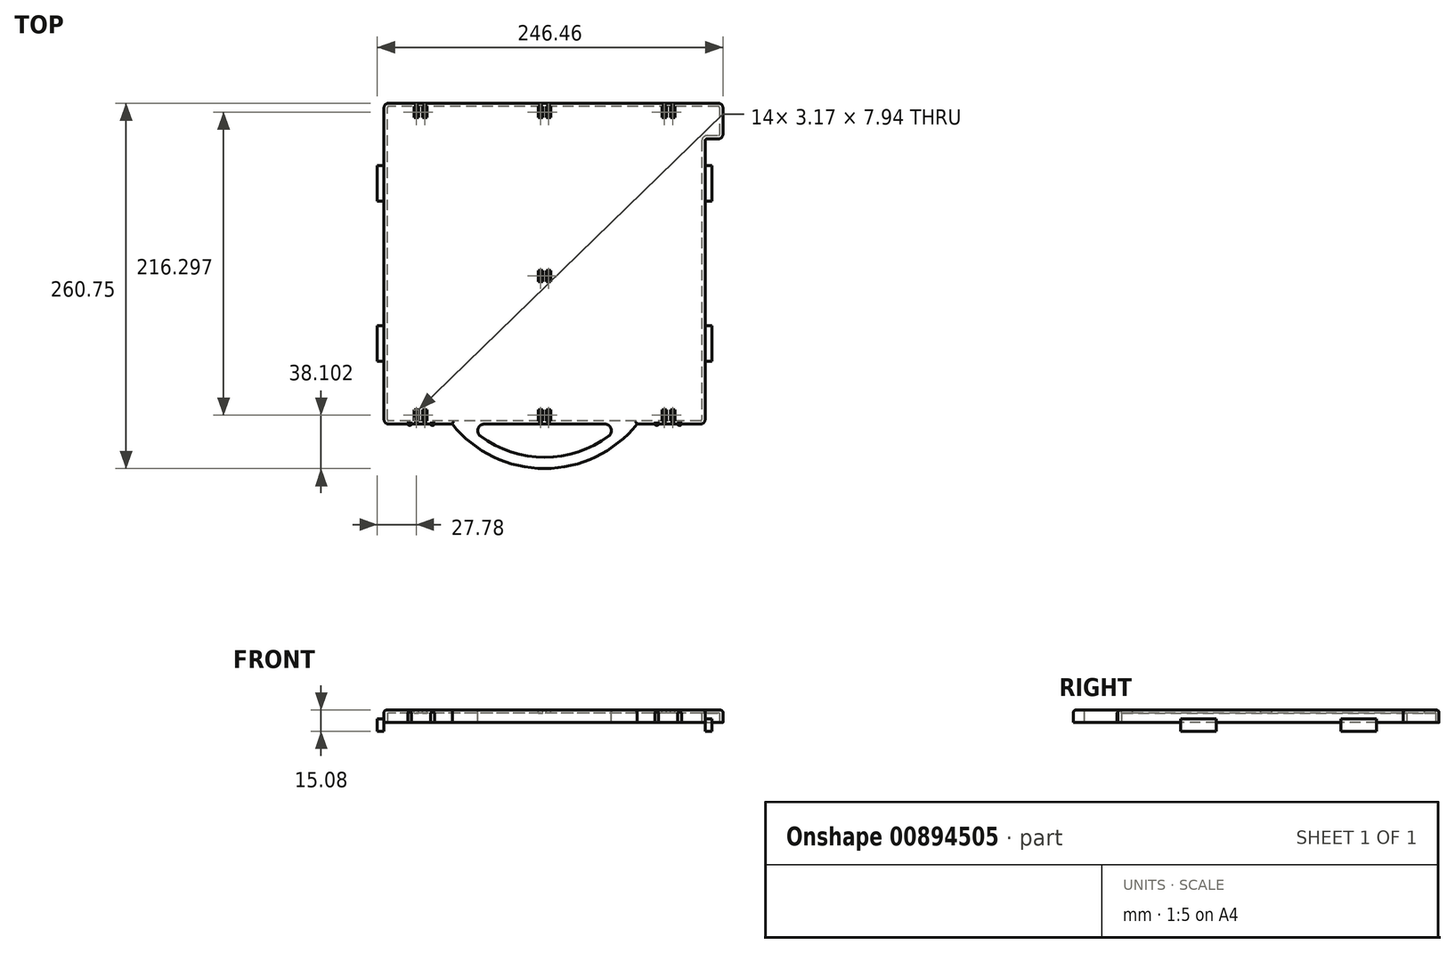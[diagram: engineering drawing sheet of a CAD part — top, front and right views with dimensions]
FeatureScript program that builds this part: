
annotation { "Feature Type Name" : "Feature", "Feature Type Description" : "" }
export const myFeature = defineFeature(function(context is Context, id is Id, definition is map)
    precondition{}
    {
        {
            var Q0;
            Q0=qCreatedBy(makeId("Top.planeOp"),FACE);
            var sketch = newSketch(context, id + "F0", { "sketchPlane" : qUnion([Q0])});
            skLineSegment(sketch, "E0.bottom", {"start": v(114.5, 114.5) * mm, "end": v(-114.5, 114.5) * mm});
            skLineSegment(sketch, "E0.top", {"start": v(114.5, -114.5) * mm, "end": v(-114.5, -114.5) * mm});
            skLineSegment(sketch, "E0.left", {"start": v(114.5, 114.5) * mm, "end": v(114.5, -114.5) * mm});
            skLineSegment(sketch, "E0.right", {"start": v(-114.5, 114.5) * mm, "end": v(-114.5, -114.5) * mm});
            skPoint(sketch, "E0.middle", {"position": v(0, 0) * mm});
            skLineSegment(sketch, "E1.bottom", {"start": v(114.5, 114.5) * mm, "end": v(127.2, 114.5) * mm});
            skLineSegment(sketch, "E1.top", {"start": v(114.5, 89.1) * mm, "end": v(127.2, 89.1) * mm});
            skLineSegment(sketch, "E1.left", {"start": v(114.5, 114.5) * mm, "end": v(114.5, 89.1) * mm});
            skLineSegment(sketch, "E1.right", {"start": v(127.2, 114.5) * mm, "end": v(127.2, 89.1) * mm});
            skSolve(sketch);
        }
        {
            var Q0;
            Q0 = qSketchRegion(id + "F0", true);
            extrude(context, id + "F1", {"entities" : qUnion([Q0]), "depth" : 8.9 * mm, "offsetDistance" : 25 * mm});
        }
        {
            var Q0;
            Q0=makeQuery(id+"F1.opExtrude","SWEPT_EDGE",EDGE,{"disambiguationData":[OSD([sQuery(id+"F0.wireOp",EDGE,"E1.bottom"),sQuery(id+"F0.wireOp",EDGE,"E1.right")])]});
            var Q1;
            Q1=makeQuery(id+"F1.opExtrude","SWEPT_EDGE",EDGE,{"disambiguationData":[OSD([sQuery(id+"F0.wireOp",EDGE,"E1.top"),sQuery(id+"F0.wireOp",EDGE,"E1.right")])]});
            var Q2;
            Q2=makeQuery(id+"F1.opExtrude","SWEPT_EDGE",EDGE,{"disambiguationData":[OSD([sQuery(id+"F0.wireOp",EDGE,"E0.bottom"),sQuery(id+"F0.wireOp",EDGE,"E0.right")])]});
            var Q3;
            Q3=makeQuery(id+"F1.opExtrude","SWEPT_EDGE",EDGE,{"disambiguationData":[OSD([sQuery(id+"F0.wireOp",EDGE,"E0.top"),sQuery(id+"F0.wireOp",EDGE,"E0.right")])]});
            var Q4;
            Q4=makeQuery(id+"F1.opExtrude","SWEPT_EDGE",EDGE,{"disambiguationData":[OSD([sQuery(id+"F0.wireOp",EDGE,"E0.top"),sQuery(id+"F0.wireOp",EDGE,"E0.left")])]});
            fillet(context, id + "F2", {"entities" : qUnion([Q0, Q1, Q2, Q3, Q4]), "radius" : 3.17 * mm, "tangentPropagation" : true, "allowEdgeOverflow" : false});
        }
        {
            var Q0;
            Q0=makeQuery(id+"F1.opExtrude","SWEPT_EDGE",EDGE,{"disambiguationData":[OSD([sQuery(id+"F0.wireOp",EDGE,"E0.left"),sQuery(id+"F0.wireOp",EDGE,"E1.top"),sQuery(id+"F0.wireOp",EDGE,"E1.left")])]});
            fillet(context, id + "F3", {"entities" : qUnion([Q0]), "radius" : 1.59 * mm, "tangentPropagation" : true, "allowEdgeOverflow" : false});
        }
        {
            var Q0;
            Q0=makeQuery(id+"F1.opExtrude","CAP_FACE",FACE,{"disambiguationData":[OSD([sQuery(id+"F0.wireOp",EDGE,"E0.bottom"),sQuery(id+"F0.wireOp",EDGE,"E0.top"),sQuery(id+"F0.wireOp",EDGE,"E0.left"),sQuery(id+"F0.wireOp",EDGE,"E0.right"),sQuery(id+"F0.wireOp",EDGE,"E1.bottom"),sQuery(id+"F0.wireOp",EDGE,"E1.top"),sQuery(id+"F0.wireOp",EDGE,"E1.right")])],"isStart":false});
            var sketch = newSketch(context, id + "F4", { "sketchPlane" : qUnion([Q0])});
            skLineSegment(sketch, "E2", {"start": v(0, 0) * mm, "end": v(0, 114.5) * mm, "construction": true});
            skLineSegment(sketch, "E3", {"start": v(0, 0) * mm, "end": v(0, -114.5) * mm, "construction": true});
            skLineSegment(sketch, "E4.bottom", {"start": v(-1.39, 112.12) * mm, "end": v(-4.56, 112.12) * mm});
            skLineSegment(sketch, "E4.top", {"start": v(-1.39, 104.18) * mm, "end": v(-4.56, 104.18) * mm});
            skLineSegment(sketch, "E4.left", {"start": v(-1.39, 112.12) * mm, "end": v(-1.39, 104.18) * mm});
            skLineSegment(sketch, "E4.right", {"start": v(-4.56, 112.12) * mm, "end": v(-4.56, 104.18) * mm});
            skLineSegment(sketch, "E5", {"start": v(-4.56, 112.12) * mm, "end": v(-83.94, 112.12) * mm, "construction": true});
            skLineSegment(sketch, "E6.bottom", {"start": v(-83.94, 112.12) * mm, "end": v(-87.11, 112.12) * mm});
            skLineSegment(sketch, "E6.top", {"start": v(-83.94, 104.18) * mm, "end": v(-87.11, 104.18) * mm});
            skLineSegment(sketch, "E6.left", {"start": v(-83.94, 112.12) * mm, "end": v(-83.94, 104.18) * mm});
            skLineSegment(sketch, "E6.right", {"start": v(-87.11, 112.12) * mm, "end": v(-87.11, 104.18) * mm});
            skLineSegment(sketch, "E7.bottom", {"start": v(-89.9, 112.12) * mm, "end": v(-93.07, 112.12) * mm});
            skLineSegment(sketch, "E7.top", {"start": v(-89.9, 104.18) * mm, "end": v(-93.07, 104.18) * mm});
            skLineSegment(sketch, "E7.left", {"start": v(-89.9, 112.12) * mm, "end": v(-89.9, 104.18) * mm});
            skLineSegment(sketch, "E7.right", {"start": v(-93.07, 112.12) * mm, "end": v(-93.07, 104.18) * mm});
            skLineSegment(sketch, "E8.MirrorCS", {"start": v(83.94, 112.12) * mm, "end": v(87.11, 112.12) * mm});
            skLineSegment(sketch, "E9.MirrorCS", {"start": v(1.39, 112.12) * mm, "end": v(4.56, 112.12) * mm});
            skLineSegment(sketch, "E10.MirrorCS", {"start": v(1.39, 112.12) * mm, "end": v(1.39, 104.18) * mm});
            skLineSegment(sketch, "E11.MirrorCS", {"start": v(89.9, 104.18) * mm, "end": v(93.07, 104.18) * mm});
            skLineSegment(sketch, "E12.MirrorCS", {"start": v(89.9, 112.12) * mm, "end": v(89.9, 104.18) * mm});
            skLineSegment(sketch, "E13.MirrorCS", {"start": v(4.56, 112.12) * mm, "end": v(4.56, 104.18) * mm});
            skLineSegment(sketch, "E14.MirrorCS", {"start": v(89.9, 112.12) * mm, "end": v(93.07, 112.12) * mm});
            skLineSegment(sketch, "E15.MirrorCS", {"start": v(83.94, 104.18) * mm, "end": v(87.11, 104.18) * mm});
            skLineSegment(sketch, "E16.MirrorCS", {"start": v(83.94, 112.12) * mm, "end": v(83.94, 104.18) * mm});
            skLineSegment(sketch, "E17.MirrorCS", {"start": v(87.11, 112.12) * mm, "end": v(87.11, 104.18) * mm});
            skLineSegment(sketch, "E18.MirrorCS", {"start": v(93.07, 112.12) * mm, "end": v(93.07, 104.18) * mm});
            skLineSegment(sketch, "E19.MirrorCS", {"start": v(1.39, 104.18) * mm, "end": v(4.56, 104.18) * mm});
            skLineSegment(sketch, "E20.MirrorCS", {"start": v(4.56, 112.12) * mm, "end": v(83.94, 112.12) * mm, "construction": true});
            skLineSegment(sketch, "E21", {"start": v(0, 0) * mm, "end": v(114.5, 0) * mm, "construction": true});
            skLineSegment(sketch, "E22.MirrorCS", {"start": v(-1.39, -104.18) * mm, "end": v(-4.56, -104.18) * mm});
            skLineSegment(sketch, "E23.MirrorCS", {"start": v(-83.94, -104.18) * mm, "end": v(-87.11, -104.18) * mm});
            skLineSegment(sketch, "E24.MirrorCS", {"start": v(1.39, -104.18) * mm, "end": v(4.56, -104.18) * mm});
            skLineSegment(sketch, "E25.MirrorCS", {"start": v(-1.39, -112.12) * mm, "end": v(-4.56, -112.12) * mm});
            skLineSegment(sketch, "E26.MirrorCS", {"start": v(-83.94, -112.12) * mm, "end": v(-87.11, -112.12) * mm});
            skLineSegment(sketch, "E27.MirrorCS", {"start": v(-87.11, -112.12) * mm, "end": v(-87.11, -104.18) * mm});
            skLineSegment(sketch, "E28.MirrorCS", {"start": v(-4.56, -112.12) * mm, "end": v(-4.56, -104.18) * mm});
            skLineSegment(sketch, "E29.MirrorCS", {"start": v(-89.9, -112.12) * mm, "end": v(-89.9, -104.18) * mm});
            skLineSegment(sketch, "E30.MirrorCS", {"start": v(83.94, -112.12) * mm, "end": v(87.11, -112.12) * mm});
            skLineSegment(sketch, "E31.MirrorCS", {"start": v(-83.94, -112.12) * mm, "end": v(-83.94, -104.18) * mm});
            skLineSegment(sketch, "E32.MirrorCS", {"start": v(1.39, -112.12) * mm, "end": v(4.56, -112.12) * mm});
            skLineSegment(sketch, "E33.MirrorCS", {"start": v(-89.9, -112.12) * mm, "end": v(-93.07, -112.12) * mm});
            skLineSegment(sketch, "E34.MirrorCS", {"start": v(1.39, -112.12) * mm, "end": v(1.39, -104.18) * mm});
            skLineSegment(sketch, "E35.MirrorCS", {"start": v(4.56, -112.12) * mm, "end": v(4.56, -104.18) * mm});
            skLineSegment(sketch, "E36.MirrorCS", {"start": v(-1.39, -112.12) * mm, "end": v(-1.39, -104.18) * mm});
            skLineSegment(sketch, "E37.MirrorCS", {"start": v(89.9, -104.18) * mm, "end": v(93.07, -104.18) * mm});
            skLineSegment(sketch, "E38.MirrorCS", {"start": v(89.9, -112.12) * mm, "end": v(89.9, -104.18) * mm});
            skLineSegment(sketch, "E39.MirrorCS", {"start": v(93.07, -112.12) * mm, "end": v(93.07, -104.18) * mm});
            skLineSegment(sketch, "E40.MirrorCS", {"start": v(83.94, -104.18) * mm, "end": v(87.11, -104.18) * mm});
            skLineSegment(sketch, "E41.MirrorCS", {"start": v(89.9, -112.12) * mm, "end": v(93.07, -112.12) * mm});
            skLineSegment(sketch, "E42.MirrorCS", {"start": v(83.94, -112.12) * mm, "end": v(83.94, -104.18) * mm});
            skLineSegment(sketch, "E43.MirrorCS", {"start": v(-89.9, -104.18) * mm, "end": v(-93.07, -104.18) * mm});
            skLineSegment(sketch, "E44.MirrorCS", {"start": v(-93.07, -112.12) * mm, "end": v(-93.07, -104.18) * mm});
            skLineSegment(sketch, "E45.MirrorCS", {"start": v(87.11, -112.12) * mm, "end": v(87.11, -104.18) * mm});
            skLineSegment(sketch, "E46.MirrorCS", {"start": v(-4.56, -112.12) * mm, "end": v(-83.94, -112.12) * mm, "construction": true});
            skLineSegment(sketch, "E47.MirrorCS", {"start": v(4.56, -112.12) * mm, "end": v(83.94, -112.12) * mm, "construction": true});
            skLineSegment(sketch, "E48.MirrorCS", {"start": v(-1.39, -4.8) * mm, "end": v(-4.56, -4.8) * mm});
            skLineSegment(sketch, "E49.MirrorCS", {"start": v(1.39, -4.8) * mm, "end": v(4.56, -4.8) * mm});
            skLineSegment(sketch, "E50.MirrorCS", {"start": v(-1.39, -12.74) * mm, "end": v(-4.56, -12.74) * mm});
            skLineSegment(sketch, "E51.MirrorCS", {"start": v(-4.56, -12.74) * mm, "end": v(-4.56, -4.8) * mm});
            skLineSegment(sketch, "E52.MirrorCS", {"start": v(1.39, -12.74) * mm, "end": v(4.56, -12.74) * mm});
            skLineSegment(sketch, "E53.MirrorCS", {"start": v(1.39, -12.74) * mm, "end": v(1.39, -4.8) * mm});
            skLineSegment(sketch, "E54.MirrorCS", {"start": v(4.56, -12.74) * mm, "end": v(4.56, -4.8) * mm});
            skLineSegment(sketch, "E55.MirrorCS", {"start": v(-1.39, -12.74) * mm, "end": v(-1.39, -4.8) * mm});
            skLineSegment(sketch, "E56", {"start": v(-1.39, -8.77) * mm, "end": v(1.39, -8.77) * mm, "construction": true});
            skPoint(sketch, "E57", {"position": v(0, -8.77) * mm});
            skLineSegment(sketch, "E58", {"start": v(-1.39, 108.15) * mm, "end": v(1.39, 108.15) * mm, "construction": true});
            skSolve(sketch);
        }
        {
            var Q0;
            Q0 = qSketchRegion(id + "F4", true);
            extrude(context, id + "F5", {"entities" : qUnion([Q0]), "operationType" : NewBodyOperationType.REMOVE, "endBound" : BoundingType.THROUGH_ALL, "oppositeDirection" : true, "depth" : 25.4 * mm, "offsetDistance" : 25.4 * mm});
        }
        {
            var Q0;
            Q0=makeQuery(id+"F1.opExtrude","SWEPT_FACE",FACE,{"disambiguationData":[OSD([sQuery(id+"F0.wireOp",EDGE,"E0.top")])]});
            var sketch = newSketch(context, id + "F6", { "sketchPlane" : qUnion([Q0])});
            skLineSegment(sketch, "E59.bottom", {"start": v(-97.63, 0) * mm, "end": v(-94.85, 0) * mm});
            skLineSegment(sketch, "E59.top", {"start": v(-97.63, 7.34) * mm, "end": v(-94.85, 7.34) * mm});
            skLineSegment(sketch, "E59.left", {"start": v(-97.63, 0) * mm, "end": v(-97.63, 7.34) * mm});
            skLineSegment(sketch, "E59.right", {"start": v(-94.85, 0) * mm, "end": v(-94.85, 7.34) * mm});
            skLineSegment(sketch, "E60.bottom", {"start": v(-81.36, 0) * mm, "end": v(-78.58, 0) * mm});
            skLineSegment(sketch, "E60.top", {"start": v(-81.36, 7.34) * mm, "end": v(-78.58, 7.34) * mm});
            skLineSegment(sketch, "E60.left", {"start": v(-81.36, 0) * mm, "end": v(-81.36, 7.34) * mm});
            skLineSegment(sketch, "E60.right", {"start": v(-78.58, 0) * mm, "end": v(-78.58, 7.34) * mm});
            skLineSegment(sketch, "E61", {"start": v(0, 0) * mm, "end": v(0, 8.9) * mm, "construction": true});
            skLineSegment(sketch, "E62.MirrorCS", {"start": v(97.63, 0) * mm, "end": v(94.85, 0) * mm});
            skLineSegment(sketch, "E63.MirrorCS", {"start": v(81.36, 0) * mm, "end": v(78.58, 0) * mm});
            skLineSegment(sketch, "E64.MirrorCS", {"start": v(94.85, 0) * mm, "end": v(94.85, 7.34) * mm});
            skLineSegment(sketch, "E65.MirrorCS", {"start": v(81.36, 7.34) * mm, "end": v(78.58, 7.34) * mm});
            skLineSegment(sketch, "E66.MirrorCS", {"start": v(78.58, 0) * mm, "end": v(78.58, 7.34) * mm});
            skLineSegment(sketch, "E67.MirrorCS", {"start": v(81.36, 0) * mm, "end": v(81.36, 7.34) * mm});
            skLineSegment(sketch, "E68.MirrorCS", {"start": v(97.63, 0) * mm, "end": v(97.63, 7.34) * mm});
            skLineSegment(sketch, "E69.MirrorCS", {"start": v(97.63, 7.34) * mm, "end": v(94.85, 7.34) * mm});
            skSolve(sketch);
        }
        {
            var Q0;
            Q0 = qSketchRegion(id + "F6", true);
            extrude(context, id + "F7", {"entities" : qUnion([Q0]), "operationType" : NewBodyOperationType.ADD, "depth" : 0.8 * mm, "offsetDistance" : 25.4 * mm});
        }
        {
            var Q0;
            Q0=makeQuery(id+"F7.opExtrude","CAP_EDGE",EDGE,{"disambiguationData":[OSD([sQuery(id+"F6.wireOp",EDGE,"E66.MirrorCS")])],"isStart":false});
            var Q1;
            Q1=makeQuery(id+"F7.opExtrude","CAP_EDGE",EDGE,{"disambiguationData":[OSD([sQuery(id+"F6.wireOp",EDGE,"E67.MirrorCS")])],"isStart":false});
            var Q2;
            Q2=makeQuery(id+"F7.opExtrude","SWEPT_EDGE",EDGE,{"disambiguationData":[OSD([sQuery(id+"F6.wireOp",EDGE,"E65.MirrorCS"),sQuery(id+"F6.wireOp",EDGE,"E67.MirrorCS")])]});
            var Q3;
            Q3=makeQuery(id+"F7.opExtrude","SWEPT_EDGE",EDGE,{"disambiguationData":[OSD([sQuery(id+"F6.wireOp",EDGE,"E65.MirrorCS"),sQuery(id+"F6.wireOp",EDGE,"E66.MirrorCS")])]});
            var Q4;
            Q4=makeQuery(id+"F7.opExtrude","CAP_EDGE",EDGE,{"disambiguationData":[OSD([sQuery(id+"F6.wireOp",EDGE,"E65.MirrorCS")])],"isStart":false});
            var Q5;
            Q5=makeQuery(id+"F7.opExtrude","SWEPT_EDGE",EDGE,{"disambiguationData":[OSD([sQuery(id+"F6.wireOp",EDGE,"E68.MirrorCS"),sQuery(id+"F6.wireOp",EDGE,"E69.MirrorCS")])]});
            var Q6;
            Q6=makeQuery(id+"F7.opExtrude","SWEPT_EDGE",EDGE,{"disambiguationData":[OSD([sQuery(id+"F6.wireOp",EDGE,"E64.MirrorCS"),sQuery(id+"F6.wireOp",EDGE,"E69.MirrorCS")])]});
            var Q7;
            Q7=makeQuery(id+"F7.opExtrude","CAP_EDGE",EDGE,{"disambiguationData":[OSD([sQuery(id+"F6.wireOp",EDGE,"E69.MirrorCS")])],"isStart":false});
            var Q8;
            Q8=makeQuery(id+"F7.opExtrude","CAP_EDGE",EDGE,{"disambiguationData":[OSD([sQuery(id+"F6.wireOp",EDGE,"E68.MirrorCS")])],"isStart":false});
            var Q9;
            Q9=makeQuery(id+"F7.opExtrude","CAP_EDGE",EDGE,{"disambiguationData":[OSD([sQuery(id+"F6.wireOp",EDGE,"E64.MirrorCS")])],"isStart":false});
            var Q10;
            Q10=makeQuery(id+"F7.opExtrude","SWEPT_EDGE",EDGE,{"disambiguationData":[OSD([sQuery(id+"F6.wireOp",EDGE,"E59.top"),sQuery(id+"F6.wireOp",EDGE,"E59.left")])]});
            var Q11;
            Q11=makeQuery(id+"F7.opExtrude","SWEPT_EDGE",EDGE,{"disambiguationData":[OSD([sQuery(id+"F6.wireOp",EDGE,"E59.top"),sQuery(id+"F6.wireOp",EDGE,"E59.right")])]});
            var Q12;
            Q12=makeQuery(id+"F7.opExtrude","SWEPT_EDGE",EDGE,{"disambiguationData":[OSD([sQuery(id+"F6.wireOp",EDGE,"E60.top"),sQuery(id+"F6.wireOp",EDGE,"E60.left")])]});
            var Q13;
            Q13=makeQuery(id+"F7.opExtrude","SWEPT_EDGE",EDGE,{"disambiguationData":[OSD([sQuery(id+"F6.wireOp",EDGE,"E60.top"),sQuery(id+"F6.wireOp",EDGE,"E60.right")])]});
            var Q14;
            Q14=makeQuery(id+"F7.opExtrude","CAP_EDGE",EDGE,{"disambiguationData":[OSD([sQuery(id+"F6.wireOp",EDGE,"E60.top")])],"isStart":false});
            var Q15;
            Q15=makeQuery(id+"F7.opExtrude","CAP_EDGE",EDGE,{"disambiguationData":[OSD([sQuery(id+"F6.wireOp",EDGE,"E59.top")])],"isStart":false});
            var Q16;
            Q16=makeQuery(id+"F7.opExtrude","CAP_EDGE",EDGE,{"disambiguationData":[OSD([sQuery(id+"F6.wireOp",EDGE,"E59.left")])],"isStart":false});
            var Q17;
            Q17=makeQuery(id+"F7.opExtrude","CAP_EDGE",EDGE,{"disambiguationData":[OSD([sQuery(id+"F6.wireOp",EDGE,"E60.left")])],"isStart":false});
            var Q18;
            Q18=makeQuery(id+"F7.opExtrude","CAP_EDGE",EDGE,{"disambiguationData":[OSD([sQuery(id+"F6.wireOp",EDGE,"E60.right")])],"isStart":false});
            var Q19;
            Q19=makeQuery(id+"F7.opExtrude","CAP_EDGE",EDGE,{"disambiguationData":[OSD([sQuery(id+"F6.wireOp",EDGE,"E59.right")])],"isStart":false});
            fillet(context, id + "F8", {"entities" : qUnion([Q0, Q1, Q2, Q3, Q4, Q5, Q6, Q7, Q8, Q9, Q10, Q11, Q12, Q13, Q14, Q15, Q16, Q17, Q18, Q19]), "radius" : 0.8 * mm, "tangentPropagation" : true, "allowEdgeOverflow" : false});
        }
        {
            var Q0;
            Q0=makeQuery(id+"F1.opExtrude","SWEPT_FACE",FACE,{"disambiguationData":[OSD([sQuery(id+"F0.wireOp",EDGE,"E0.left")])]});
            var sketch = newSketch(context, id + "F9", { "sketchPlane" : qUnion([Q0])});
            skLineSegment(sketch, "E70.bottom", {"start": v(44.65, 2.54) * mm, "end": v(70.05, 2.54) * mm});
            skLineSegment(sketch, "E70.top", {"start": v(44.65, -6.2) * mm, "end": v(70.05, -6.2) * mm});
            skLineSegment(sketch, "E70.left", {"start": v(44.65, 2.54) * mm, "end": v(44.65, -6.2) * mm});
            skLineSegment(sketch, "E70.right", {"start": v(70.05, 2.54) * mm, "end": v(70.05, -6.2) * mm});
            skLineSegment(sketch, "E71.bottom", {"start": v(-69.65, 2.54) * mm, "end": v(-44.25, 2.54) * mm});
            skLineSegment(sketch, "E71.top", {"start": v(-69.65, -6.2) * mm, "end": v(-44.25, -6.2) * mm});
            skLineSegment(sketch, "E71.left", {"start": v(-69.65, 2.54) * mm, "end": v(-69.65, -6.2) * mm});
            skLineSegment(sketch, "E71.right", {"start": v(-44.25, 2.54) * mm, "end": v(-44.25, -6.2) * mm});
            skLineSegment(sketch, "E72", {"start": v(44.65, 2.54) * mm, "end": v(-44.25, 2.54) * mm, "construction": true});
            skSolve(sketch);
        }
        {
            var Q0;
            Q0 = qSketchRegion(id + "F9", true);
            extrude(context, id + "F10", {"entities" : qUnion([Q0]), "operationType" : NewBodyOperationType.ADD, "depth" : 4.76 * mm, "offsetDistance" : 25.4 * mm});
        }
        {
            var Q0;
            Q0=makeQuery(id+"F1.opExtrude","SWEPT_FACE",FACE,{"disambiguationData":[OSD([sQuery(id+"F0.wireOp",EDGE,"E0.right")])]});
            var sketch = newSketch(context, id + "F11", { "sketchPlane" : qUnion([Q0])});
            skLineSegment(sketch, "E73.0", {"start": v(-44.65, 2.54) * mm, "end": v(-70.05, 2.54) * mm});
            skLineSegment(sketch, "E73.1", {"start": v(-44.65, -6.2) * mm, "end": v(-70.05, -6.2) * mm});
            skLineSegment(sketch, "E73.2", {"start": v(-44.65, 2.54) * mm, "end": v(-44.65, -6.2) * mm});
            skLineSegment(sketch, "E73.3", {"start": v(-70.05, 2.54) * mm, "end": v(-70.05, -6.2) * mm});
            skLineSegment(sketch, "E73.4", {"start": v(69.65, 2.54) * mm, "end": v(44.25, 2.54) * mm});
            skLineSegment(sketch, "E73.5", {"start": v(69.65, -6.2) * mm, "end": v(44.25, -6.2) * mm});
            skLineSegment(sketch, "E73.6", {"start": v(69.65, 2.54) * mm, "end": v(69.65, -6.2) * mm});
            skLineSegment(sketch, "E73.7", {"start": v(44.25, 2.54) * mm, "end": v(44.25, -6.2) * mm});
            skLineSegment(sketch, "E73.8", {"start": v(-44.65, 2.54) * mm, "end": v(44.25, 2.54) * mm});
            skSolve(sketch);
        }
        {
            var Q0;
            Q0 = qSketchRegion(id + "F11", true);
            extrude(context, id + "F12", {"entities" : qUnion([Q0]), "operationType" : NewBodyOperationType.ADD, "depth" : 4.76 * mm, "offsetDistance" : 25.4 * mm});
        }
        {
            var Q0;
            Q0=makeQuery(id+"F1.opExtrude","CAP_FACE",FACE,{"disambiguationData":[OSD([sQuery(id+"F0.wireOp",EDGE,"E0.bottom"),sQuery(id+"F0.wireOp",EDGE,"E0.top"),sQuery(id+"F0.wireOp",EDGE,"E0.left"),sQuery(id+"F0.wireOp",EDGE,"E0.right"),sQuery(id+"F0.wireOp",EDGE,"E1.bottom"),sQuery(id+"F0.wireOp",EDGE,"E1.top"),sQuery(id+"F0.wireOp",EDGE,"E1.right")])],"isStart":false});
            var sketch = newSketch(context, id + "F13", { "sketchPlane" : qUnion([Q0])});
            skPoint(sketch, "E74.0", {"position": v(-78.58, -114.5) * mm});
            skPoint(sketch, "E75.0", {"position": v(78.58, -114.5) * mm});
            skLineSegment(sketch, "E76", {"start": v(-78.58, -114.5) * mm, "end": v(-65.88, -114.5) * mm});
            skLineSegment(sketch, "E77", {"start": v(78.58, -114.5) * mm, "end": v(65.88, -114.5) * mm});
            skLineSegment(sketch, "E78.bottom", {"start": v(-65.88, -114.5) * mm, "end": v(65.88, -114.5) * mm});
            skLineSegment(sketch, "E78.top", {"start": v(-65.88, -146.25) * mm, "end": v(65.88, -146.25) * mm});
            skLineSegment(sketch, "E78.left", {"start": v(-65.88, -114.5) * mm, "end": v(-65.88, -146.25) * mm});
            skLineSegment(sketch, "E78.right", {"start": v(65.88, -114.5) * mm, "end": v(65.88, -146.25) * mm});
            skLineSegment(sketch, "E79", {"start": v(0, -146.25) * mm, "end": v(0, -62.02) * mm, "construction": true});
            skLineSegment(sketch, "E80", {"start": v(0, -62.02) * mm, "end": v(-65.88, -114.5) * mm, "construction": true});
            skLineSegment(sketch, "E81", {"start": v(0, -62.02) * mm, "end": v(65.88, -114.5) * mm, "construction": true});
            skArc(sketch, "E82", {"start": v(65.88, -114.5) * mm, "mid": v(0, -146.25) * mm, "end": v(-65.88, -114.5) * mm});
            skLineSegment(sketch, "E83", {"start": v(0, -62.02) * mm, "end": v(0, -138.31) * mm, "construction": true});
            skArc(sketch, "E84", {"start": v(0, -138.31) * mm, "mid": v(30.14, -132.1) * mm, "end": v(55.37, -114.5) * mm});
            skArc(sketch, "E85", {"start": v(0, -138.31) * mm, "mid": v(-30.14, -132.1) * mm, "end": v(-55.37, -114.5) * mm});
            skSolve(sketch);
        }
        {
            var Q0;
            {var subQ6=sQuery(id+"F13.wireOp",EDGE,"E84");Q0=makeQuery(id+"F13.imprint","IMPRINT",FACE,{"disambiguationData":[TD([[makeQuery(id+"F13.imprint","IMPRINT",EDGE,{"derivedFrom":subQ6}),-1.0]])]});}
            var Q1;
            Q1=makeQuery(id+"F7.boolean.opBoolean","MERGE",FACE,{"derivedFrom":[makeQuery(id+"F1.opExtrude","CAP_FACE",FACE,{"disambiguationData":[OSD([sQuery(id+"F0.wireOp",EDGE,"E0.bottom"),sQuery(id+"F0.wireOp",EDGE,"E0.top"),sQuery(id+"F0.wireOp",EDGE,"E0.left"),sQuery(id+"F0.wireOp",EDGE,"E0.right"),sQuery(id+"F0.wireOp",EDGE,"E1.bottom"),sQuery(id+"F0.wireOp",EDGE,"E1.top"),sQuery(id+"F0.wireOp",EDGE,"E1.right")])],"isStart":true}),makeQuery(id+"F7.opExtrude","SWEPT_FACE",FACE,{"disambiguationData":[OSD([sQuery(id+"F6.wireOp",EDGE,"E59.bottom")])]}),makeQuery(id+"F7.opExtrude","SWEPT_FACE",FACE,{"disambiguationData":[OSD([sQuery(id+"F6.wireOp",EDGE,"E60.bottom")])]}),makeQuery(id+"F7.opExtrude","SWEPT_FACE",FACE,{"disambiguationData":[OSD([sQuery(id+"F6.wireOp",EDGE,"E62.MirrorCS")])]}),makeQuery(id+"F7.opExtrude","SWEPT_FACE",FACE,{"disambiguationData":[OSD([sQuery(id+"F6.wireOp",EDGE,"E63.MirrorCS")])]})]});
            extrude(context, id + "F14", {"entities" : qUnion([Q0]), "operationType" : NewBodyOperationType.ADD, "endBound" : BoundingType.UP_TO_SURFACE, "oppositeDirection" : true, "depth" : 25.4 * mm, "endBoundEntityFace" : qUnion([Q1]), "offsetDistance" : 25.4 * mm});
        }
        {
            var Q0;
            Q0=makeQuery(id+"F14.opExtrude","SWEPT_EDGE",EDGE,{"disambiguationData":[OSD([sQuery(id+"F13.wireOp",EDGE,"E78.bottom"),sQuery(id+"F13.wireOp",EDGE,"E85")])]});
            var Q1;
            Q1=makeQuery(id+"F14.opExtrude","SWEPT_EDGE",EDGE,{"disambiguationData":[OSD([sQuery(id+"F13.wireOp",EDGE,"E78.bottom"),sQuery(id+"F13.wireOp",EDGE,"E84")])]});
            fillet(context, id + "F15", {"entities" : qUnion([Q0, Q1]), "radius" : 4.76 * mm, "tangentPropagation" : true, "allowEdgeOverflow" : false});
        }
        {
            var Q0;
            Q0=makeQuery(id+"F14.opExtrude","CAP_EDGE",EDGE,{"disambiguationData":[OSD([sQuery(id+"F13.wireOp",EDGE,"E84"),sQuery(id+"F13.wireOp",EDGE,"E85")])],"isStart":true});
            var Q1;
            {var subQ1=sQuery(id+"F0.wireOp",EDGE,"E0.left");var subQ2=sQuery(id+"F0.wireOp",EDGE,"E0.top");Q1=makeQuery(id+"F14.boolean.opBoolean","SPLIT",EDGE,{"disambiguationData":[TD([makeQuery(id+"F2.opFillet","BLEND_FACE",FACE,{"disambiguationData":[OSD([subQ2,subQ1])]})])],"derivedFrom":makeQuery(id+"F1.opExtrude","CAP_EDGE",EDGE,{"disambiguationData":[OSD([subQ2])],"isStart":false})});}
            var Q2;
            Q2=makeQuery(id+"F14.opExtrude","CAP_EDGE",EDGE,{"disambiguationData":[OSD([sQuery(id+"F13.wireOp",EDGE,"E82")])],"isStart":true});
            fillet(context, id + "F16", {"entities" : qUnion([Q0, Q1, Q2]), "radius" : 1.59 * mm, "tangentPropagation" : true, "allowEdgeOverflow" : false});
        }
        {
            var Q0;
            Q0=makeQuery(id+"F14.boolean.opBoolean","MERGE",FACE,{"derivedFrom":[makeQuery(id+"F7.boolean.opBoolean","MERGE",FACE,{"derivedFrom":[makeQuery(id+"F1.opExtrude","CAP_FACE",FACE,{"disambiguationData":[OSD([sQuery(id+"F0.wireOp",EDGE,"E0.bottom"),sQuery(id+"F0.wireOp",EDGE,"E0.top"),sQuery(id+"F0.wireOp",EDGE,"E0.left"),sQuery(id+"F0.wireOp",EDGE,"E0.right"),sQuery(id+"F0.wireOp",EDGE,"E1.bottom"),sQuery(id+"F0.wireOp",EDGE,"E1.top"),sQuery(id+"F0.wireOp",EDGE,"E1.right")])],"isStart":true}),makeQuery(id+"F7.opExtrude","SWEPT_FACE",FACE,{"disambiguationData":[OSD([sQuery(id+"F6.wireOp",EDGE,"E59.bottom")])]}),makeQuery(id+"F7.opExtrude","SWEPT_FACE",FACE,{"disambiguationData":[OSD([sQuery(id+"F6.wireOp",EDGE,"E60.bottom")])]}),makeQuery(id+"F7.opExtrude","SWEPT_FACE",FACE,{"disambiguationData":[OSD([sQuery(id+"F6.wireOp",EDGE,"E62.MirrorCS")])]}),makeQuery(id+"F7.opExtrude","SWEPT_FACE",FACE,{"disambiguationData":[OSD([sQuery(id+"F6.wireOp",EDGE,"E63.MirrorCS")])]})]}),makeQuery(id+"F14.opExtrude","CAP_FACE",FACE,{"disambiguationData":[OSD([sQuery(id+"F13.wireOp",EDGE,"E78.bottom"),sQuery(id+"F13.wireOp",EDGE,"E82"),sQuery(id+"F13.wireOp",EDGE,"E84"),sQuery(id+"F13.wireOp",EDGE,"E85")])],"isStart":false})]});
            var sketch = newSketch(context, id + "F17", { "sketchPlane" : qUnion([Q0])});
            skLineSegment(sketch, "E86.0", {"start": v(-97.63, 114.5) * mm, "end": v(-111.32, 114.5) * mm});
            skLineSegment(sketch, "E86.1", {"start": v(-114.5, 69.65) * mm, "end": v(-114.5, 111.32) * mm});
            skLineSegment(sketch, "E86.2", {"start": v(-81.36, 114.5) * mm, "end": v(-94.85, 114.5) * mm});
            skLineSegment(sketch, "E86.3", {"start": v(-65.88, 114.5) * mm, "end": v(-78.58, 114.5) * mm});
            skLineSegment(sketch, "E86.4", {"start": v(42.9, 114.5) * mm, "end": v(-42.9, 114.5) * mm});
            skLineSegment(sketch, "E86.5", {"start": v(78.58, 114.5) * mm, "end": v(65.88, 114.5) * mm});
            skLineSegment(sketch, "E86.6", {"start": v(94.85, 114.5) * mm, "end": v(81.36, 114.5) * mm});
            skLineSegment(sketch, "E86.7", {"start": v(111.32, 114.5) * mm, "end": v(97.63, 114.5) * mm});
            skLineSegment(sketch, "E86.8", {"start": v(114.5, 69.65) * mm, "end": v(114.5, 111.32) * mm});
            skLineSegment(sketch, "E86.9", {"start": v(114.5, -44.65) * mm, "end": v(114.5, 44.25) * mm});
            skLineSegment(sketch, "E86.10", {"start": v(-114.5, -44.65) * mm, "end": v(-114.5, 44.25) * mm});
            skLineSegment(sketch, "E86.11", {"start": v(-114.5, -111.32) * mm, "end": v(-114.5, -70.05) * mm});
            skLineSegment(sketch, "E86.12", {"start": v(124.02, -114.5) * mm, "end": v(-111.32, -114.5) * mm});
            skLineSegment(sketch, "E86.13", {"start": v(127.2, -111.32) * mm, "end": v(127.2, -92.27) * mm});
            skLineSegment(sketch, "E86.14", {"start": v(116.09, -89.1) * mm, "end": v(124.02, -89.1) * mm});
            skLineSegment(sketch, "E86.15", {"start": v(114.5, -87.51) * mm, "end": v(114.5, -70.05) * mm});
            skArc(sketch, "E87.0", {"start": v(-111.32, 114.5) * mm, "mid": v(-113.57, 113.57) * mm, "end": v(-114.5, 111.32) * mm});
            skArc(sketch, "E88.0", {"start": v(-111.32, 112.15) * mm, "mid": v(-111.9, 111.9) * mm, "end": v(-112.15, 111.32) * mm});
            skArc(sketch, "E89.0", {"start": v(112.15, 111.32) * mm, "mid": v(111.9, 111.9) * mm, "end": v(111.32, 112.15) * mm});
            skArc(sketch, "E90.0", {"start": v(124.85, -92.27) * mm, "mid": v(124.6, -91.7) * mm, "end": v(124.02, -91.45) * mm});
            skArc(sketch, "E91.0", {"start": v(124.02, -112.15) * mm, "mid": v(124.6, -111.9) * mm, "end": v(124.85, -111.32) * mm});
            skArc(sketch, "E92.0", {"start": v(116.09, -91.45) * mm, "mid": v(113.3, -90.3) * mm, "end": v(112.15, -87.51) * mm});
            skArc(sketch, "E93.0", {"start": v(-112.15, -111.32) * mm, "mid": v(-111.9, -111.9) * mm, "end": v(-111.32, -112.15) * mm});
            skLineSegment(sketch, "E94.0", {"start": v(120.66, -112.15) * mm, "end": v(-111.32, -112.15) * mm});
            skLineSegment(sketch, "E95.0", {"start": v(-112.15, -44.65) * mm, "end": v(-112.15, 44.25) * mm});
            skLineSegment(sketch, "E96", {"start": v(-112.15, 111.32) * mm, "end": v(-112.15, 44.25) * mm});
            skLineSegment(sketch, "E97", {"start": v(-112.15, -44.65) * mm, "end": v(-112.15, -111.32) * mm});
            skLineSegment(sketch, "E98", {"start": v(124.85, -111.32) * mm, "end": v(124.85, -92.27) * mm});
            skLineSegment(sketch, "E99", {"start": v(116.09, -91.45) * mm, "end": v(124.02, -91.45) * mm});
            skLineSegment(sketch, "E100", {"start": v(120.66, -112.15) * mm, "end": v(124.02, -112.15) * mm});
            skLineSegment(sketch, "E101", {"start": v(112.15, -87.51) * mm, "end": v(112.15, 111.32) * mm});
            skLineSegment(sketch, "E102", {"start": v(111.32, 112.15) * mm, "end": v(-111.32, 112.15) * mm});
            skSolve(sketch);
        }
        {
            var Q0;
            Q0 = qSketchRegion(id + "F17", true);
            var Q1;
            Q1=makeQuery(id+"F14.boolean.opBoolean","MERGE",FACE,{"derivedFrom":[makeQuery(id+"F1.opExtrude","CAP_FACE",FACE,{"disambiguationData":[OSD([sQuery(id+"F0.wireOp",EDGE,"E0.bottom"),sQuery(id+"F0.wireOp",EDGE,"E0.top"),sQuery(id+"F0.wireOp",EDGE,"E0.left"),sQuery(id+"F0.wireOp",EDGE,"E0.right"),sQuery(id+"F0.wireOp",EDGE,"E1.bottom"),sQuery(id+"F0.wireOp",EDGE,"E1.top"),sQuery(id+"F0.wireOp",EDGE,"E1.right")])],"isStart":false}),makeQuery(id+"F14.opExtrude","CAP_FACE",FACE,{"disambiguationData":[OSD([sQuery(id+"F13.wireOp",EDGE,"E78.bottom"),sQuery(id+"F13.wireOp",EDGE,"E82"),sQuery(id+"F13.wireOp",EDGE,"E84"),sQuery(id+"F13.wireOp",EDGE,"E85")])],"isStart":true})]});
            extrude(context, id + "F18", {"entities" : qUnion([Q0]), "operationType" : NewBodyOperationType.REMOVE, "endBound" : BoundingType.UP_TO_SURFACE, "oppositeDirection" : true, "depth" : 25 * mm, "endBoundEntityFace" : qUnion([Q1]), "hasOffset" : true, "offsetDistance" : 2 * mm});
        }
    });
